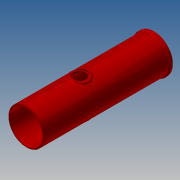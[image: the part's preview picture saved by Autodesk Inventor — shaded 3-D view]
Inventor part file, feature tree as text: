
AUTODESK INVENTOR PART (.ipt)
format: ipt  version: 2017.3 (Build 213257000, 257)  size: 337,920 bytes
history: native  units: in
note: dims shown in document units (in); Inventor stores cm internally (conversion verified against a paired STEP export)
features: extrude x10, sketch x8, fillet x3, chamfer x2, plane x2, pattern_circular x1, other x1, projected_geometry x1
ambient origin geometry x8: Origin, YZ Plane, XZ Plane, XY Plane, X Axis, Y Axis, Z Axis, Center Point
bodies: Solid1 (feature_tree)
feature tree (28):
  extrude  "Extrusion1"  Depth=31.0in
  extrude  "Extrusion2"  Depth=32.75in
  extrude  "Extrusion3"  Depth=32.48in
  chamfer  "Chamfer1"  Distance=1.0in
  extrude  "Extrusion4"  Depth=0.125in TaperAngle=45.0deg
  chamfer  "Chamfer2"  Distance=0.5in
  fillet  "Fillet1"  Radius=0.0312in
  extrude  "Extrusion5"  Depth=17.3228in
  plane  "Work Plane3"
  sketch  "Sketch7"  dims[d16=0.0312in d17=0.125in d18=45.0deg d19=0.0312in]
  extrude  "Extrusion9"  Depth=0.0312in
  extrude  "Extrusion11"  Depth=0.0312in TaperAngle=0.0deg
  sketch  "Sketch9"  dims[d22=11.1417in d23=46.9685in d24=0.5in d25=0.0in d39=15.1417in d40=1.0in d41=0.0in d42=12.75in d43=32.75in d44=110.0in d45=0.0in d48=2.0in d50=0.7874in d51=360.0deg d53=3.0in d54=1.0in d55=0.0in d56=1.0in d57=0.0in d58=0.0312in d59=0.5in d60=0.0in]
  extrude  "Extrusion12"  Depth=0.0312in
  extrude  "Extrusion13"  Depth=0.0312in TaperAngle=0.0deg
  fillet  "Fillet3"  Radius=12.75in
  fillet  "Fillet5"  Radius=32.75in
  pattern_circular  "Circular Pattern2"  [2 undecoded]
  sketch  "Sketch1"  dims[d0=28.5in d1=31.0in]
  sketch  "Sketch2"  dims[d2=110.0in d3=0.0in d4=32.75in]
  sketch  "Sketch3"  dims[d5=2.0in d6=0.0in d7=32.48in d8=1.0in d9=0.0in]
  sketch  "Sketch4"  dims[d10=0.875in d11=0.125in d12=45.0deg]
  sketch  "Sketch5"  dims[d13=29.98in d14=0.5in d15=0.0in]
  plane  "Work Plane2"
  sketch  "Sketch8"  dims[d20=2.5984in d21=17.3228in]
  other  "Srf1"
  projected_geometry  "Projected Loop1"
  extrude  "ExtrusionSrf1"  TaperAngle=0.0deg  [1 undecoded]
note: 3 required parameter values undecoded (feature->parameter linkage not recoverable at this tier; creation-order binding heuristic only, values carry confidence <= 0.55)
